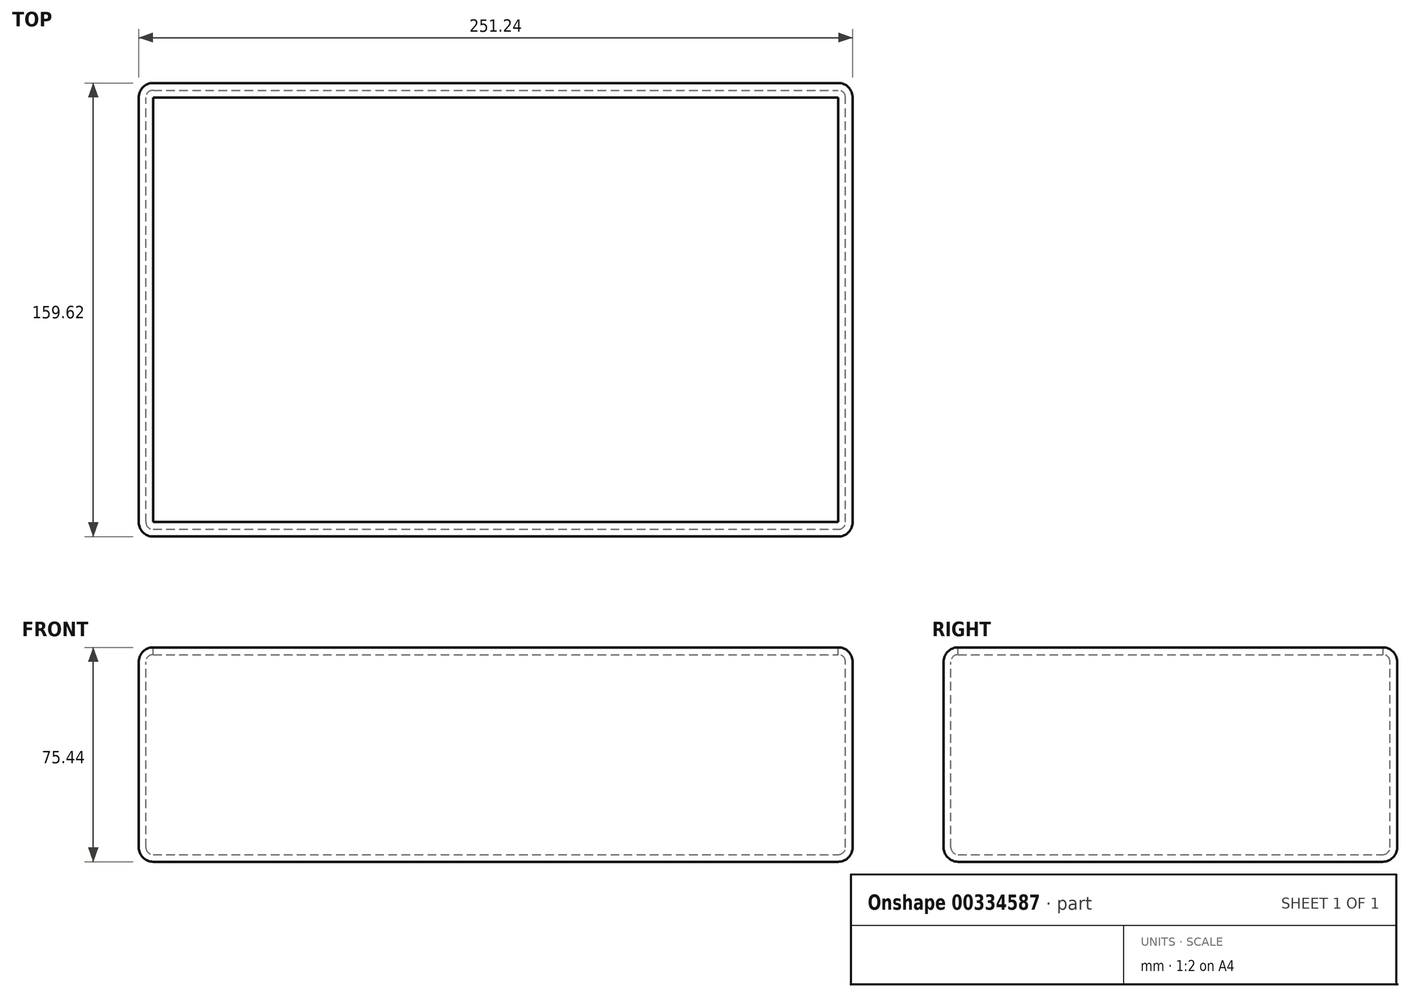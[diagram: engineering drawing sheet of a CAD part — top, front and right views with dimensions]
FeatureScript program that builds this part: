
annotation { "Feature Type Name" : "Feature", "Feature Type Description" : "" }
export const myFeature = defineFeature(function(context is Context, id is Id, definition is map)
    precondition{}
    {
        {
            var Q0;
            Q0=qCreatedBy(makeId("Top.planeOp"),FACE);
            var sketch = newSketch(context, id + "F0", { "sketchPlane" : qUnion([Q0])});
            skLineSegment(sketch, "E0.bottom", {"start": v(0, 0) * mm, "end": v(155.23, 0) * mm});
            skLineSegment(sketch, "E0.top", {"start": v(0, 82.4) * mm, "end": v(155.23, 82.4) * mm});
            skLineSegment(sketch, "E0.left", {"start": v(0, 0) * mm, "end": v(0, 82.4) * mm});
            skLineSegment(sketch, "E0.right", {"start": v(155.23, 0) * mm, "end": v(155.23, 82.4) * mm});
            skSolve(sketch);
        }
        {
            var Q0;
            Q0=makeQuery(id+"F0.imprint","IMPRINT",FACE,{"disambiguationData":[TD([[makeQuery(id+"F0.imprint","IMPRINT",EDGE,{"derivedFrom":sQuery(id+"F0.wireOp",EDGE,"E0.bottom")}),1.0]])]});
            extrude(context, id + "F1", {"entities" : qUnion([Q0]), "depth" : 75.44 * mm});
        }
        {
            var Q0;
            Q0=makeQuery(id+"F1.opExtrude","SWEPT_FACE",FACE,{"disambiguationData":[OSD([sQuery(id+"F0.wireOp",EDGE,"E0.bottom")])]});
            extrude(context, id + "F2", {"entities" : qUnion([Q0]), "operationType" : NewBodyOperationType.ADD, "depth" : 77.22 * mm});
        }
        {
            var Q0;
            {var subQ0=sQuery(id+"F0.wireOp",EDGE,"E0.left");Q0=makeQuery(id+"F2.boolean.opBoolean","MERGE",FACE,{"derivedFrom":[makeQuery(id+"F1.opExtrude","SWEPT_FACE",FACE,{"disambiguationData":[OSD([subQ0])]}),makeQuery(id+"F2.opExtrude","SWEPT_FACE",FACE,{"disambiguationData":[OSD([sQuery(id+"F0.wireOp",EDGE,"E0.bottom"),subQ0])]})]});}
            extrude(context, id + "F3", {"entities" : qUnion([Q0]), "operationType" : NewBodyOperationType.ADD, "depth" : 96.01 * mm});
        }
        {
            var Q0;
            {var subQ0=sQuery(id+"F0.wireOp",EDGE,"E0.left");var subQ1=sQuery(id+"F0.wireOp",EDGE,"E0.bottom");Q0=makeQuery(id+"F3.opExtrude","CAP_EDGE",EDGE,{"disambiguationData":[OSD([subQ1,subQ0]),TDD([makeQuery(id+"F2.boolean.opBoolean","MERGE",EDGE,{"derivedFrom":[makeQuery(id+"F1.opExtrude","CAP_EDGE",EDGE,{"disambiguationData":[OSD([subQ0])],"isStart":false}),makeQuery(id+"F2.opExtrude","SWEPT_EDGE",EDGE,{"disambiguationData":[OSD([subQ1,subQ0]),TDD([makeQuery(id+"F1.opExtrude","CAP_VERTEX",VERTEX,{"disambiguationData":[OSD([subQ1,subQ0])],"isStart":false})])]})]})])],"isStart":false});}
            var Q1;
            {var subQ0=sQuery(id+"F0.wireOp",EDGE,"E0.left");var subQ1=sQuery(id+"F0.wireOp",EDGE,"E0.bottom");Q1=makeQuery(id+"F3.boolean.opBoolean","MERGE",EDGE,{"derivedFrom":[makeQuery(id+"F2.opExtrude","CAP_EDGE",EDGE,{"disambiguationData":[OSD([subQ1]),TDD([makeQuery(id+"F1.opExtrude","CAP_EDGE",EDGE,{"disambiguationData":[OSD([subQ1])],"isStart":false})])],"isStart":false}),makeQuery(id+"F3.opExtrude","SWEPT_EDGE",EDGE,{"disambiguationData":[OSD([subQ1,subQ0]),TDD([makeQuery(id+"F2.opExtrude","CAP_VERTEX",VERTEX,{"disambiguationData":[OSD([subQ1,subQ0]),TDD([makeQuery(id+"F1.opExtrude","CAP_VERTEX",VERTEX,{"disambiguationData":[OSD([subQ1,subQ0])],"isStart":false})])],"isStart":false})])]})]});}
            var Q2;
            {var subQ0=sQuery(id+"F0.wireOp",EDGE,"E0.left");var subQ1=sQuery(id+"F0.wireOp",EDGE,"E0.bottom");Q2=makeQuery(id+"F3.boolean.opBoolean","MERGE",EDGE,{"derivedFrom":[makeQuery(id+"F2.opExtrude","CAP_EDGE",EDGE,{"disambiguationData":[OSD([subQ1]),TDD([makeQuery(id+"F1.opExtrude","CAP_EDGE",EDGE,{"disambiguationData":[OSD([subQ1])],"isStart":true})])],"isStart":false}),makeQuery(id+"F3.opExtrude","SWEPT_EDGE",EDGE,{"disambiguationData":[OSD([subQ1,subQ0]),TDD([makeQuery(id+"F2.opExtrude","CAP_VERTEX",VERTEX,{"disambiguationData":[OSD([subQ1,subQ0]),TDD([makeQuery(id+"F1.opExtrude","CAP_VERTEX",VERTEX,{"disambiguationData":[OSD([subQ1,subQ0])],"isStart":true})])],"isStart":false})])]})]});}
            var Q3;
            {var subQ0=sQuery(id+"F0.wireOp",EDGE,"E0.left");var subQ1=sQuery(id+"F0.wireOp",EDGE,"E0.bottom");Q3=makeQuery(id+"F3.opExtrude","CAP_EDGE",EDGE,{"disambiguationData":[OSD([subQ1,subQ0]),TDD([makeQuery(id+"F2.opExtrude","CAP_EDGE",EDGE,{"disambiguationData":[OSD([subQ1,subQ0])],"isStart":false})])],"isStart":false});}
            var Q4;
            {var subQ0=sQuery(id+"F0.wireOp",EDGE,"E0.left");var subQ1=sQuery(id+"F0.wireOp",EDGE,"E0.bottom");Q4=makeQuery(id+"F3.opExtrude","CAP_EDGE",EDGE,{"disambiguationData":[OSD([subQ1,subQ0]),TDD([makeQuery(id+"F2.boolean.opBoolean","MERGE",EDGE,{"derivedFrom":[makeQuery(id+"F1.opExtrude","CAP_EDGE",EDGE,{"disambiguationData":[OSD([subQ0])],"isStart":true}),makeQuery(id+"F2.opExtrude","SWEPT_EDGE",EDGE,{"disambiguationData":[OSD([subQ1,subQ0]),TDD([makeQuery(id+"F1.opExtrude","CAP_VERTEX",VERTEX,{"disambiguationData":[OSD([subQ1,subQ0])],"isStart":true})])]})]})])],"isStart":false});}
            var Q5;
            {var subQ0=sQuery(id+"F0.wireOp",EDGE,"E0.left");var subQ1=sQuery(id+"F0.wireOp",EDGE,"E0.top");Q5=makeQuery(id+"F3.boolean.opBoolean","MERGE",EDGE,{"derivedFrom":[makeQuery(id+"F1.opExtrude","CAP_EDGE",EDGE,{"disambiguationData":[OSD([subQ1])],"isStart":false}),makeQuery(id+"F3.opExtrude","SWEPT_EDGE",EDGE,{"disambiguationData":[OSD([subQ1,subQ0]),TDD([makeQuery(id+"F1.opExtrude","CAP_VERTEX",VERTEX,{"disambiguationData":[OSD([subQ1,subQ0])],"isStart":false})])]})]});}
            var Q6;
            {var subQ0=sQuery(id+"F0.wireOp",EDGE,"E0.right");var subQ1=sQuery(id+"F0.wireOp",EDGE,"E0.bottom");Q6=makeQuery(id+"F2.boolean.opBoolean","MERGE",EDGE,{"derivedFrom":[makeQuery(id+"F1.opExtrude","CAP_EDGE",EDGE,{"disambiguationData":[OSD([subQ0])],"isStart":false}),makeQuery(id+"F2.opExtrude","SWEPT_EDGE",EDGE,{"disambiguationData":[OSD([subQ1,subQ0]),TDD([makeQuery(id+"F1.opExtrude","CAP_VERTEX",VERTEX,{"disambiguationData":[OSD([subQ1,subQ0])],"isStart":false})])]})]});}
            var Q7;
            Q7=makeQuery(id+"F2.opExtrude","CAP_EDGE",EDGE,{"disambiguationData":[OSD([sQuery(id+"F0.wireOp",EDGE,"E0.bottom"),sQuery(id+"F0.wireOp",EDGE,"E0.right")])],"isStart":false});
            var Q8;
            Q8=makeQuery(id+"F3.opExtrude","CAP_EDGE",EDGE,{"disambiguationData":[OSD([sQuery(id+"F0.wireOp",EDGE,"E0.top"),sQuery(id+"F0.wireOp",EDGE,"E0.left")])],"isStart":false});
            var Q9;
            {var subQ0=sQuery(id+"F0.wireOp",EDGE,"E0.left");var subQ1=sQuery(id+"F0.wireOp",EDGE,"E0.top");Q9=makeQuery(id+"F3.boolean.opBoolean","MERGE",EDGE,{"derivedFrom":[makeQuery(id+"F1.opExtrude","CAP_EDGE",EDGE,{"disambiguationData":[OSD([subQ1])],"isStart":true}),makeQuery(id+"F3.opExtrude","SWEPT_EDGE",EDGE,{"disambiguationData":[OSD([subQ1,subQ0]),TDD([makeQuery(id+"F1.opExtrude","CAP_VERTEX",VERTEX,{"disambiguationData":[OSD([subQ1,subQ0])],"isStart":true})])]})]});}
            var Q10;
            Q10=makeQuery(id+"F1.opExtrude","SWEPT_EDGE",EDGE,{"disambiguationData":[OSD([sQuery(id+"F0.wireOp",EDGE,"E0.top"),sQuery(id+"F0.wireOp",EDGE,"E0.right")])]});
            var Q11;
            {var subQ0=sQuery(id+"F0.wireOp",EDGE,"E0.right");var subQ1=sQuery(id+"F0.wireOp",EDGE,"E0.bottom");Q11=makeQuery(id+"F2.boolean.opBoolean","MERGE",EDGE,{"derivedFrom":[makeQuery(id+"F1.opExtrude","CAP_EDGE",EDGE,{"disambiguationData":[OSD([subQ0])],"isStart":true}),makeQuery(id+"F2.opExtrude","SWEPT_EDGE",EDGE,{"disambiguationData":[OSD([subQ1,subQ0]),TDD([makeQuery(id+"F1.opExtrude","CAP_VERTEX",VERTEX,{"disambiguationData":[OSD([subQ1,subQ0])],"isStart":true})])]})]});}
            fillet(context, id + "F4", {"entities" : qUnion([Q0, Q1, Q2, Q3, Q4, Q5, Q6, Q7, Q8, Q9, Q10, Q11]), "radius" : 5.08 * mm, "tangentPropagation" : true, "allowEdgeOverflow" : false});
        }
        {
            var Q0;
            {var subQ0=sQuery(id+"F0.wireOp",EDGE,"E0.left");var subQ1=sQuery(id+"F0.wireOp",EDGE,"E0.bottom");Q0=makeQuery(id+"F3.boolean.opBoolean","MERGE",FACE,{"derivedFrom":[makeQuery(id+"F2.boolean.opBoolean","MERGE",FACE,{"derivedFrom":[makeQuery(id+"F1.opExtrude","CAP_FACE",FACE,{"disambiguationData":[OSD([subQ1,sQuery(id+"F0.wireOp",EDGE,"E0.top"),subQ0,sQuery(id+"F0.wireOp",EDGE,"E0.right")])],"isStart":false}),makeQuery(id+"F2.opExtrude","SWEPT_FACE",FACE,{"disambiguationData":[OSD([subQ1]),TDD([makeQuery(id+"F1.opExtrude","CAP_EDGE",EDGE,{"disambiguationData":[OSD([subQ1])],"isStart":false})])]})]}),makeQuery(id+"F3.opExtrude","SWEPT_FACE",FACE,{"disambiguationData":[OSD([subQ1,subQ0]),TDD([makeQuery(id+"F2.boolean.opBoolean","MERGE",EDGE,{"derivedFrom":[makeQuery(id+"F1.opExtrude","CAP_EDGE",EDGE,{"disambiguationData":[OSD([subQ0])],"isStart":false}),makeQuery(id+"F2.opExtrude","SWEPT_EDGE",EDGE,{"disambiguationData":[OSD([subQ1,subQ0]),TDD([makeQuery(id+"F1.opExtrude","CAP_VERTEX",VERTEX,{"disambiguationData":[OSD([subQ1,subQ0])],"isStart":false})])]})]})])]})]});}
            shell(context, id + "F5", {"entities" : qUnion([Q0]), "thickness" : 2.54 * mm});
        }
        {
            var Q0;
            {var subQ0=sQuery(id+"F0.wireOp",EDGE,"E0.right");Q0=makeQuery(id+"F2.boolean.opBoolean","MERGE",FACE,{"derivedFrom":[makeQuery(id+"F1.opExtrude","SWEPT_FACE",FACE,{"disambiguationData":[OSD([subQ0])]}),makeQuery(id+"F2.opExtrude","SWEPT_FACE",FACE,{"disambiguationData":[OSD([sQuery(id+"F0.wireOp",EDGE,"E0.bottom"),subQ0])]})]});}
            var sketch = newSketch(context, id + "F6", { "sketchPlane" : qUnion([Q0])});
            skCircle(sketch, "E1", {"center": v(0, 37.72) * mm, "radius": 16.8 * mm});
            skPoint(sketch, "E1.centerSnap0", {"position": v(77.32, 37.72) * mm});
            skSolve(sketch);
        }
        {
            var Q0;
            Q0=makeQuery(id+"F6.imprint","IMPRINT",FACE,{"disambiguationData":[TD([[makeQuery(id+"F6.imprint","IMPRINT",EDGE,{"derivedFrom":sQuery(id+"F6.wireOp",EDGE,"E1")}),1.0]])]});
            var Q1;
            {var subQ0=sQuery(id+"F0.wireOp",EDGE,"E0.right");var subQ1=sQuery(id+"F0.wireOp",EDGE,"E0.bottom");Q1=makeQuery(id+"F5.opShell","OFFSET_FACE",FACE,{"disambiguationData":[OSD([subQ1,subQ0]),TDD([makeQuery(id+"F2.boolean.opBoolean","MERGE",FACE,{"derivedFrom":[makeQuery(id+"F1.opExtrude","SWEPT_FACE",FACE,{"disambiguationData":[OSD([subQ0])]}),makeQuery(id+"F2.opExtrude","SWEPT_FACE",FACE,{"disambiguationData":[OSD([subQ1,subQ0])]})]})])]});}
            extrude(context, id + "F7", {"entities" : qUnion([Q0]), "operationType" : NewBodyOperationType.ADD, "endBound" : BoundingType.UP_TO_SURFACE, "oppositeDirection" : true, "endBoundEntityFace" : qUnion([Q1]), "depth" : 25.4 * mm});
        }
    });
